# Revit family: 304_283409d322044e8dba8a30d68fed8b
name_source: partatom
category: Pipe Accessories
revit_build: Autodesk Revit 2018 (Build: 20170223_1515(x64)
units: mm (PartAtom-declared; Revit-internal decimal feet)

## family parameters
Always vertical = Yes
Cut with Voids When Loaded = No
Part Type = Valve - Breaks Into
Round Connector Dimension = Use Diameter
Shared = No
Work Plane-Based = No

## types (7) — shared parameters
CAT0 = Yes
Description = Variable orifice bronze double regulating valve PN25
H4 = 20 mm  [stored 0.0656168 ft]
HWR = 35 mm  [stored 0.114829 ft]
L2D = 77 mm
L2D_Min = 3048 mm
L3 = 10 mm  [stored 0.0328084 ft]
L6 = 2 mm  [stored 0.00656168 ft]
L7 = 36 mm  [stored 0.11811 ft]
Manufacturer = VIR
NUT1 = No
QmdConnectorList = 301;D;302;D
R5 = 20 mm  [stored 0.0656168 ft]
R6 = 8 mm  [stored 0.0262467 ft]
R7 = 9 mm  [stored 0.0295276 ft]
URL = http://www.vironline.com
W2D = 10 mm  [stored 0.0328084 ft]
magiPartTypeId = 304
magiProductFamilyId = 283409d322044e8dba8a30d68fed8b

## per-type parameters (varying)
| type | CenSd_RN2_6 | CenSd_RN_6 | D | H1 | H2 | H3 | H5 | H6 | H7 | H8 | L1 | L1__ve | L2 | L2__ve | L4 | L_2 | R1 | R2 | R3 | R4 | RN | RN2 | magiProductId |
| 9505 DN10 | 11 mm  [stored 0.0360892 ft] | 14 mm  [stored 0.0459318 ft] | 10 mm | 4 mm  [stored 0.0131234 ft] | 42 mm | 14 mm  [stored 0.0459318 ft] | 13 mm  [stored 0.0426509 ft] | 18 mm  [stored 0.0590551 ft] | 11 mm  [stored 0.0360892 ft] | 27 mm | 7 mm  [stored 0.0229659 ft] | -7 mm  [stored -0.0229659 ft] | 8 mm  [stored 0.0262467 ft] | -8 mm  [stored -0.0262467 ft] | 10 mm  [stored 0.0328084 ft] | 39 mm  [stored 0.127953 ft] | 10 mm  [stored 0.0328084 ft] | 13 mm  [stored 0.0426509 ft] | 11 mm  [stored 0.0360892 ft] | 11 mm  [stored 0.0360892 ft] | 16 mm | 13 mm  [stored 0.0426509 ft] | f06221e9bc9341508f66871c80ccb9 |
| 9505 DN15 | 13 mm  [stored 0.0426509 ft] | 15 mm  [stored 0.0492126 ft] | 15 mm | 5 mm  [stored 0.0164042 ft] | 41 mm  [stored 0.134514 ft] | 12 mm  [stored 0.0393701 ft] | 14 mm  [stored 0.0459318 ft] | 19 mm | 11 mm  [stored 0.0360892 ft] | 27 mm | 8 mm  [stored 0.0262467 ft] | -8 mm  [stored -0.0262467 ft] | 8 mm  [stored 0.0262467 ft] | -8 mm  [stored -0.0262467 ft] | 12 mm  [stored 0.0393701 ft] | 45 mm | 11 mm  [stored 0.0360892 ft] | 15 mm  [stored 0.0492126 ft] | 12 mm  [stored 0.0393701 ft] | 12 mm  [stored 0.0393701 ft] | 18 mm  [stored 0.0590551 ft] | 15 mm  [stored 0.0492126 ft] | 7168eb0cb4024df38c6d32127ca87d |
| 9505 DN20 | 14 mm  [stored 0.0459318 ft] | 17 mm  [stored 0.0557743 ft] | 20 mm | 6 mm  [stored 0.019685 ft] | 40 mm  [stored 0.131234 ft] | 12 mm  [stored 0.0393701 ft] | 16 mm | 21 mm | 11 mm  [stored 0.0360892 ft] | 27 mm | 9 mm  [stored 0.0295276 ft] | -9 mm  [stored -0.0295276 ft] | 8 mm  [stored 0.0262467 ft] | -8 mm  [stored -0.0262467 ft] | 13 mm  [stored 0.0426509 ft] | 51 mm | 13 mm  [stored 0.0426509 ft] | 16 mm | 14 mm  [stored 0.0459318 ft] | 14 mm  [stored 0.0459318 ft] | 20 mm  [stored 0.0656168 ft] | 17 mm  [stored 0.0557743 ft] | 82f2a7b1fa884f8cafe37fee21fa09 |
| 9505 DN25 | 16 mm | 19 mm | 25 mm | 7 mm  [stored 0.0229659 ft] | 39 mm  [stored 0.127953 ft] | 12 mm  [stored 0.0393701 ft] | 17 mm  [stored 0.0557743 ft] | 22 mm  [stored 0.0721785 ft] | 11 mm  [stored 0.0360892 ft] | 27 mm | 10 mm  [stored 0.0328084 ft] | -10 mm  [stored -0.0328084 ft] | 9 mm  [stored 0.0295276 ft] | -9 mm  [stored -0.0295276 ft] | 14 mm  [stored 0.0459318 ft] | 55 mm | 14 mm  [stored 0.0459318 ft] | 18 mm  [stored 0.0590551 ft] | 15 mm  [stored 0.0492126 ft] | 15 mm  [stored 0.0492126 ft] | 21 mm | 18 mm  [stored 0.0590551 ft] | a5bafb2d780d49b5957b650150642c |
| 9505 DN32 | 18 mm  [stored 0.0590551 ft] | 21 mm | 32 mm | 8 mm  [stored 0.0262467 ft] | 38 mm  [stored 0.124672 ft] | 53 mm | 19 mm | 24 mm  [stored 0.0787402 ft] | 14 mm  [stored 0.0459318 ft] | 35 mm  [stored 0.114829 ft] | 11 mm  [stored 0.0360892 ft] | -11 mm  [stored -0.0360892 ft] | 10 mm  [stored 0.0328084 ft] | -10 mm  [stored -0.0328084 ft] | 16 mm | 61 mm | 16 mm | 20 mm  [stored 0.0656168 ft] | 17 mm  [stored 0.0557743 ft] | 17 mm  [stored 0.0557743 ft] | 24 mm  [stored 0.0787402 ft] | 20 mm  [stored 0.0656168 ft] | a42dead6f7694bcf97a0a9ce0e311e |
| 9505 DN40 | 20 mm  [stored 0.0656168 ft] | 24 mm  [stored 0.0787402 ft] | 40 mm | 10 mm  [stored 0.0328084 ft] | 36 mm  [stored 0.11811 ft] | 53 mm | 21 mm | 26 mm  [stored 0.0853018 ft] | 14 mm  [stored 0.0459318 ft] | 35 mm  [stored 0.114829 ft] | 13 mm  [stored 0.0426509 ft] | -13 mm  [stored -0.0426509 ft] | 10 mm  [stored 0.0328084 ft] | -10 mm  [stored -0.0328084 ft] | 18 mm  [stored 0.0590551 ft] | 71 mm | 18 mm  [stored 0.0590551 ft] | 23 mm | 19 mm | 17 mm  [stored 0.0557743 ft] | 27 mm | 23 mm | 7d52969a8dcd46c581304e64bff261 |
| 9505 DN50 | 23 mm | 27 mm | 50 mm | 12 mm  [stored 0.0393701 ft] | 34 mm  [stored 0.111549 ft] | 53 mm | 24 mm  [stored 0.0787402 ft] | 29 mm  [stored 0.0951444 ft] | 14 mm  [stored 0.0459318 ft] | 35 mm  [stored 0.114829 ft] | 15 mm  [stored 0.0492126 ft] | -15 mm  [stored -0.0492126 ft] | 11 mm  [stored 0.0360892 ft] | -11 mm  [stored -0.0360892 ft] | 21 mm | 81 mm | 20 mm  [stored 0.0656168 ft] | 26 mm  [stored 0.0853018 ft] | 22 mm  [stored 0.0721785 ft] | 17 mm  [stored 0.0557743 ft] | 31 mm | 26 mm  [stored 0.0853018 ft] | 2fc06cc644084f6992b3d357430981 |

note: column(s) folded — value = type name in every type: MC Product Code

note: [stored X ft] marks values corroborated as IEEE doubles in the binary element streams (Revit-internal decimal feet)

## geometry (parser evidence)
native form markers: Sweep x1
no freeform markers — native parametric forms only
